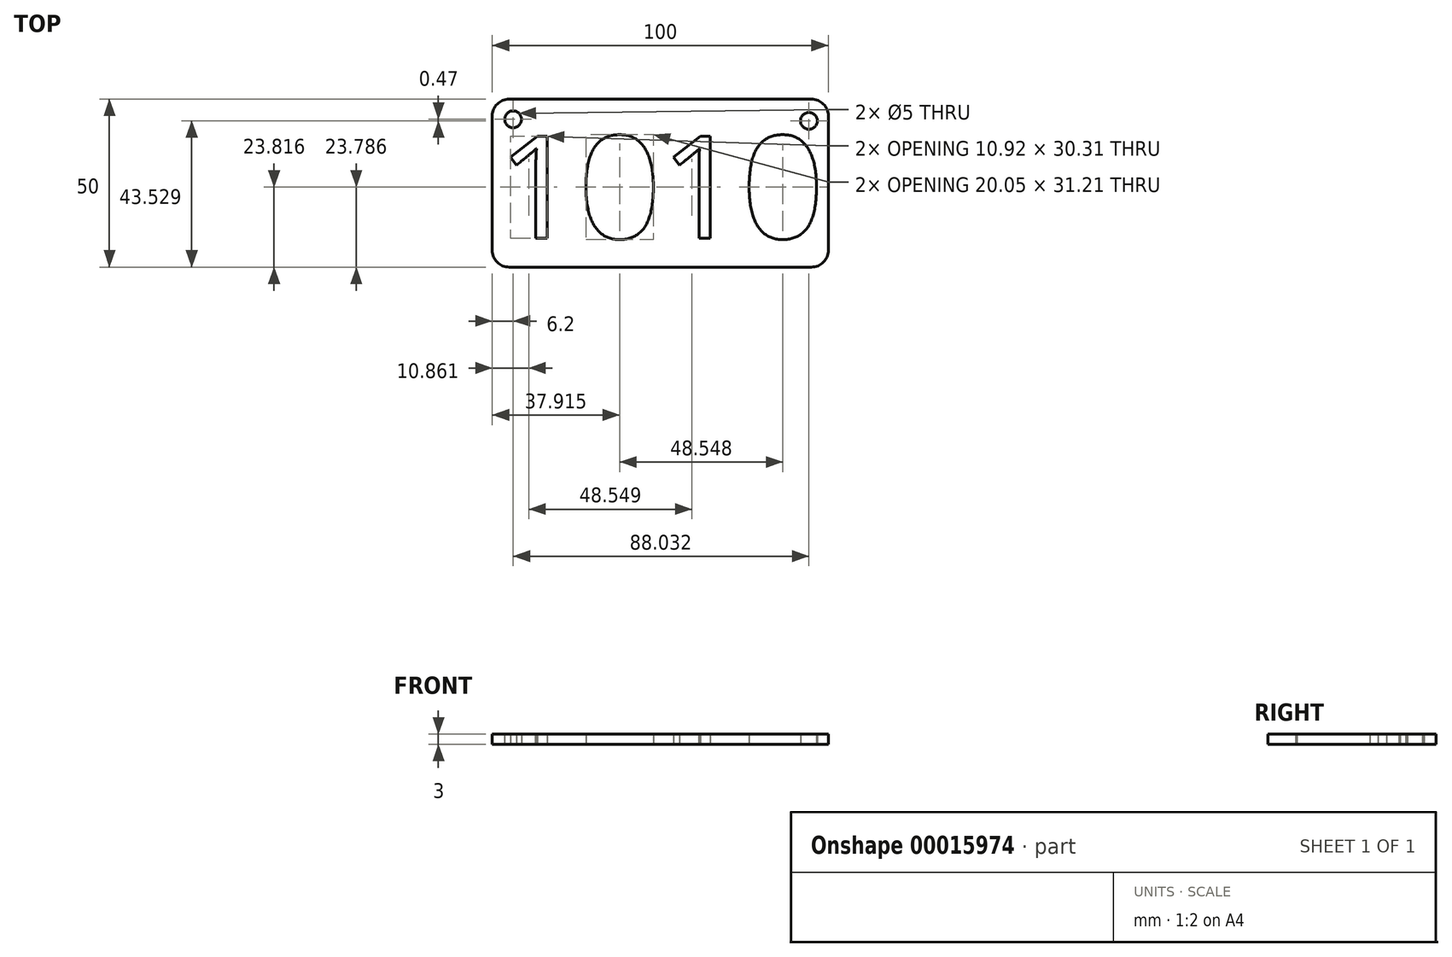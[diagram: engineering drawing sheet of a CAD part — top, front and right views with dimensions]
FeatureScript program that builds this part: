
annotation { "Feature Type Name" : "Feature", "Feature Type Description" : "" }
export const myFeature = defineFeature(function(context is Context, id is Id, definition is map)
    precondition{}
    {
        {
            var Q0;
            Q0=qCreatedBy(makeId("Top.planeOp"),FACE);
            var sketch = newSketch(context, id + "F0", { "sketchPlane" : qUnion([Q0])});
            skLineSegment(sketch, "E0.bottom", {"start": v(0, 0) * mm, "end": v(-100, 0) * mm});
            skLineSegment(sketch, "E0.top", {"start": v(0, 50) * mm, "end": v(-100, 50) * mm});
            skLineSegment(sketch, "E0.left", {"start": v(0, 0) * mm, "end": v(0, 50) * mm});
            skLineSegment(sketch, "E0.right", {"start": v(-100, 0) * mm, "end": v(-100, 50) * mm});
            skCircle(sketch, "E1", {"center": v(-93.8, 44) * mm, "radius": 2.5 * mm});
            skCircle(sketch, "E2", {"center": v(-5.77, 43.53) * mm, "radius": 2.5 * mm});
            skText(sketch, "E3", { "text": "1010", "fontName": "OpenSans-Regular.ttf"});
            const initialGuessF0  = {"E3": [-0.0985, 0.00863, 1, 0, 0.03057]};
            skSetInitialGuess(sketch, initialGuessF0);
            skSolve(sketch);
        }
        {
            var Q0;
            Q0=makeQuery(id+"F0.imprint","IMPRINT",FACE,{"disambiguationData":[TD([[makeQuery(id+"F0.imprint","IMPRINT",EDGE,{"derivedFrom":sQuery(id+"F0.wireOp",EDGE,"E0.bottom")}),-1.0]])]});
            extrude(context, id + "F1", {"entities" : qUnion([Q0]), "depth" : 3 * mm});
        }
        {
            var Q0;
            Q0=makeQuery(id+"F1.opExtrude","SWEPT_EDGE",EDGE,{"disambiguationData":[OSD([sQuery(id+"F0.wireOp",EDGE,"E0.top"),sQuery(id+"F0.wireOp",EDGE,"E0.left")])]});
            var Q1;
            Q1=makeQuery(id+"F1.opExtrude","SWEPT_EDGE",EDGE,{"disambiguationData":[OSD([sQuery(id+"F0.wireOp",EDGE,"E0.top"),sQuery(id+"F0.wireOp",EDGE,"E0.right")])]});
            var Q2;
            Q2=makeQuery(id+"F1.opExtrude","SWEPT_EDGE",EDGE,{"disambiguationData":[OSD([sQuery(id+"F0.wireOp",EDGE,"E0.bottom"),sQuery(id+"F0.wireOp",EDGE,"E0.left")])]});
            var Q3;
            Q3=makeQuery(id+"F1.opExtrude","SWEPT_EDGE",EDGE,{"disambiguationData":[OSD([sQuery(id+"F0.wireOp",EDGE,"E0.bottom"),sQuery(id+"F0.wireOp",EDGE,"E0.right")])]});
            fillet(context, id + "F2", {"entities" : qUnion([Q0, Q1, Q2, Q3]), "radius" : 5 * mm, "tangentPropagation" : true, "allowEdgeOverflow" : false});
        }
    });
